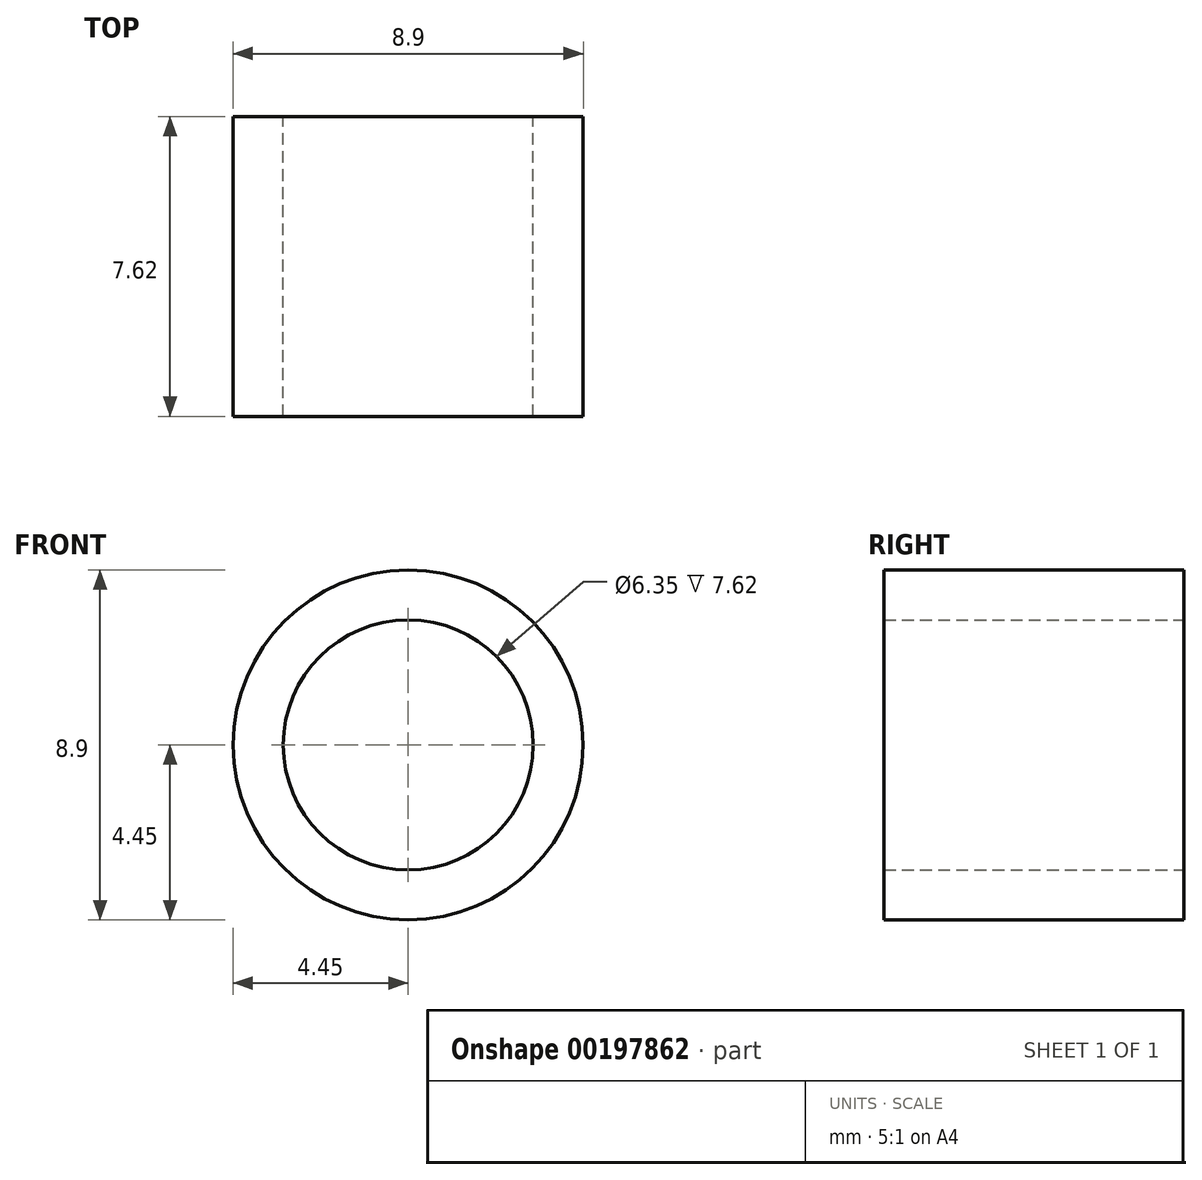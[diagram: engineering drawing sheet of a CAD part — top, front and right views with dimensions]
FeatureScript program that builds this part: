
annotation { "Feature Type Name" : "Feature", "Feature Type Description" : "" }
export const myFeature = defineFeature(function(context is Context, id is Id, definition is map)
    precondition{}
    {
        {
            var Q0;
            Q0=qCreatedBy(makeId("Front.planeOp"),FACE);
            var sketch = newSketch(context, id + "F0", { "sketchPlane" : qUnion([Q0])});
            skCircle(sketch, "E0", {"center": v(0, 0) * mm, "radius": 3.18 * mm});
            skCircle(sketch, "E1", {"center": v(0, 0) * mm, "radius": 4.45 * mm});
            skSolve(sketch);
        }
        {
            var Q0;
            Q0=makeQuery(id+"F0.imprint","IMPRINT",FACE,{"disambiguationData":[TD([[makeQuery(id+"F0.imprint","IMPRINT",EDGE,{"derivedFrom":sQuery(id+"F0.wireOp",EDGE,"E0")}),-1.0]])]});
            extrude(context, id + "F1", {"entities" : qUnion([Q0]), "depth" : 7.62 * mm});
        }
    });
